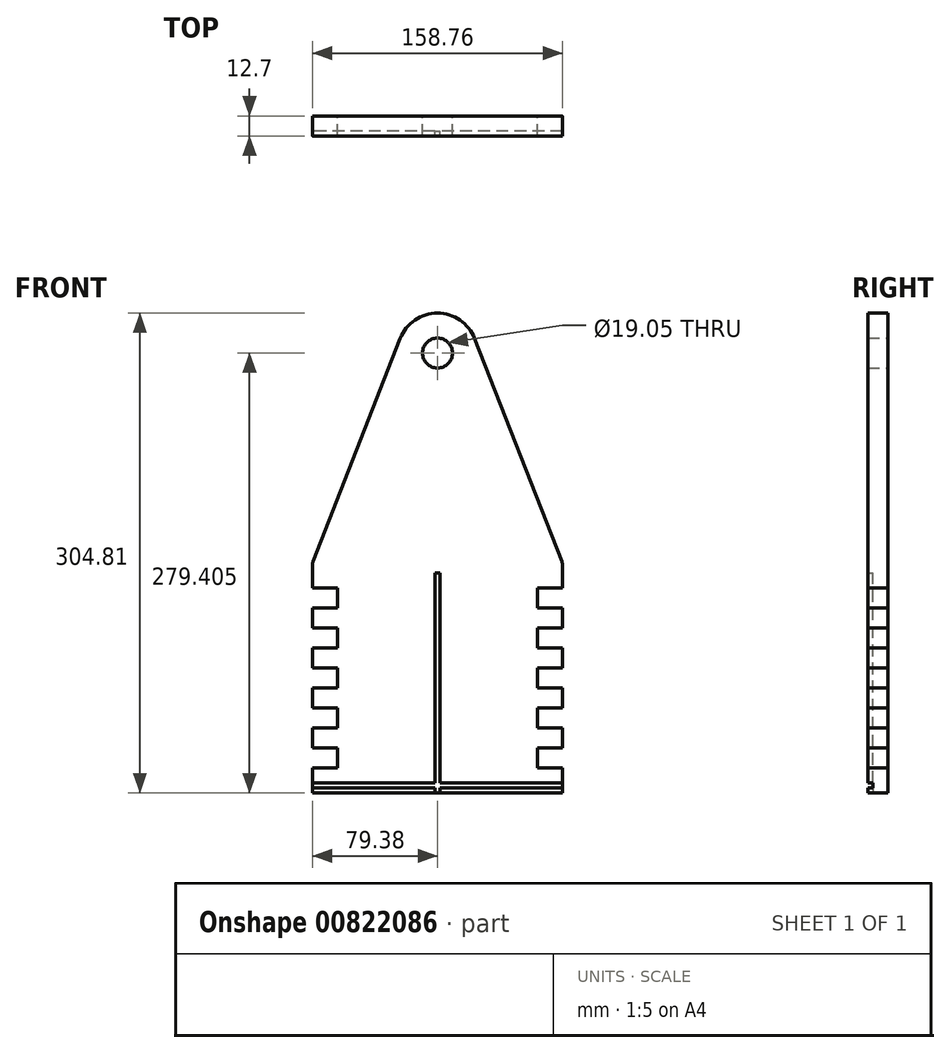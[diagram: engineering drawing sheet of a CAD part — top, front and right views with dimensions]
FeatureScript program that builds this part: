
annotation { "Feature Type Name" : "Feature", "Feature Type Description" : "" }
export const myFeature = defineFeature(function(context is Context, id is Id, definition is map)
    precondition{}
    {
        {
            var Q0;
            Q0=qCreatedBy(makeId("Front.planeOp"),FACE);
            var sketch = newSketch(context, id + "F0", { "sketchPlane" : qUnion([Q0])});
            skLineSegment(sketch, "E0.bottom", {"start": v(-79.38, -73.03) * mm, "end": v(79.38, -73.03) * mm});
            skLineSegment(sketch, "E0.left", {"start": v(-79.37, -73.03) * mm, "end": v(-79.37, -57.15) * mm});
            skLineSegment(sketch, "E0.right", {"start": v(79.38, -73.03) * mm, "end": v(79.38, -57.15) * mm});
            skPoint(sketch, "E0.middle", {"position": v(0, 0) * mm});
            skArc(sketch, "E1", {"start": v(23.66, 215.62) * mm, "mid": v(0, 231.78) * mm, "end": v(-23.66, 215.62) * mm});
            skLineSegment(sketch, "E2.bottom", {"start": v(-79.38, -57.15) * mm, "end": v(-63.5, -57.15) * mm});
            skLineSegment(sketch, "E2.top", {"start": v(-79.38, -44.45) * mm, "end": v(-63.5, -44.45) * mm});
            skLineSegment(sketch, "E2.right", {"start": v(-63.5, -57.15) * mm, "end": v(-63.5, -44.45) * mm});
            skLineSegment(sketch, "E3.0.1.0", {"start": v(-63.5, -31.75) * mm, "end": v(-63.5, -19.05) * mm});
            skLineSegment(sketch, "E3.0.1.2", {"start": v(-79.37, -31.75) * mm, "end": v(-63.5, -31.75) * mm});
            skLineSegment(sketch, "E3.0.1.3", {"start": v(-79.37, -19.05) * mm, "end": v(-63.5, -19.05) * mm});
            skLineSegment(sketch, "E3.0.2.0", {"start": v(-63.5, -6.35) * mm, "end": v(-63.5, 6.35) * mm});
            skLineSegment(sketch, "E3.0.2.2", {"start": v(-79.38, -6.35) * mm, "end": v(-63.5, -6.35) * mm});
            skLineSegment(sketch, "E3.0.2.3", {"start": v(-79.38, 6.35) * mm, "end": v(-63.5, 6.35) * mm});
            skLineSegment(sketch, "E3.0.3.0", {"start": v(-63.5, 19.05) * mm, "end": v(-63.5, 31.75) * mm});
            skLineSegment(sketch, "E3.0.3.2", {"start": v(-79.38, 19.05) * mm, "end": v(-63.5, 19.05) * mm});
            skLineSegment(sketch, "E3.0.3.3", {"start": v(-79.38, 31.75) * mm, "end": v(-63.5, 31.75) * mm});
            skLineSegment(sketch, "E3.0.4.0", {"start": v(-63.5, 44.45) * mm, "end": v(-63.5, 57.15) * mm});
            skLineSegment(sketch, "E3.0.4.2", {"start": v(-79.38, 44.45) * mm, "end": v(-63.5, 44.45) * mm});
            skLineSegment(sketch, "E3.0.4.3", {"start": v(-79.38, 57.15) * mm, "end": v(-63.5, 57.15) * mm});
            skLineSegment(sketch, "E3.direction2", {"start": v(-79.37, -44.45) * mm, "end": v(-79.37, -31.75) * mm, "construction": true});
            skLineSegment(sketch, "E4.MirrorCS", {"start": v(79.38, 44.45) * mm, "end": v(63.5, 44.45) * mm});
            skLineSegment(sketch, "E5.MirrorCS", {"start": v(79.37, -19.05) * mm, "end": v(63.5, -19.05) * mm});
            skLineSegment(sketch, "E6.MirrorCS", {"start": v(79.37, -31.75) * mm, "end": v(63.5, -31.75) * mm});
            skLineSegment(sketch, "E7.MirrorCS", {"start": v(63.5, -31.75) * mm, "end": v(63.5, -19.05) * mm});
            skLineSegment(sketch, "E8.MirrorCS", {"start": v(79.38, 31.75) * mm, "end": v(63.5, 31.75) * mm});
            skLineSegment(sketch, "E9.MirrorCS", {"start": v(79.38, 6.35) * mm, "end": v(63.5, 6.35) * mm});
            skLineSegment(sketch, "E10.MirrorCS", {"start": v(63.5, -57.15) * mm, "end": v(63.5, -44.45) * mm});
            skLineSegment(sketch, "E11.MirrorCS", {"start": v(79.38, -44.45) * mm, "end": v(63.5, -44.45) * mm});
            skLineSegment(sketch, "E12.MirrorCS", {"start": v(79.38, -57.15) * mm, "end": v(63.5, -57.15) * mm});
            skLineSegment(sketch, "E13.MirrorCS", {"start": v(79.38, -6.35) * mm, "end": v(63.5, -6.35) * mm});
            skLineSegment(sketch, "E14.MirrorCS", {"start": v(63.5, 19.05) * mm, "end": v(63.5, 31.75) * mm});
            skLineSegment(sketch, "E15.MirrorCS", {"start": v(63.5, -6.35) * mm, "end": v(63.5, 6.35) * mm});
            skLineSegment(sketch, "E16.MirrorCS", {"start": v(79.38, 19.05) * mm, "end": v(63.5, 19.05) * mm});
            skLineSegment(sketch, "E17.MirrorCS", {"start": v(63.5, 44.45) * mm, "end": v(63.5, 57.15) * mm});
            skLineSegment(sketch, "E18.MirrorCS", {"start": v(79.38, 57.15) * mm, "end": v(63.5, 57.15) * mm});
            skLineSegment(sketch, "E19.MirrorCS", {"start": v(79.37, -44.45) * mm, "end": v(79.37, -31.75) * mm, "construction": true});
            skLineSegment(sketch, "E20.trimOffspring", {"start": v(-79.38, 57.15) * mm, "end": v(-79.38, 71.83) * mm});
            skLineSegment(sketch, "E21.trimOffspring", {"start": v(-79.38, 31.75) * mm, "end": v(-79.38, 44.45) * mm});
            skLineSegment(sketch, "E22.trimOffspring", {"start": v(-79.38, 6.35) * mm, "end": v(-79.38, 19.05) * mm});
            skLineSegment(sketch, "E23.trimOffspring", {"start": v(-79.38, -19.05) * mm, "end": v(-79.38, -6.35) * mm});
            skLineSegment(sketch, "E24.trimOffspring", {"start": v(-79.37, -44.45) * mm, "end": v(-79.37, -31.75) * mm});
            skLineSegment(sketch, "E25.trimOffspring", {"start": v(79.38, -44.45) * mm, "end": v(79.38, -31.75) * mm});
            skLineSegment(sketch, "E26.trimOffspring", {"start": v(79.38, -19.05) * mm, "end": v(79.38, -6.35) * mm});
            skLineSegment(sketch, "E27.trimOffspring", {"start": v(79.38, 6.35) * mm, "end": v(79.38, 19.05) * mm});
            skLineSegment(sketch, "E28.trimOffspring", {"start": v(79.38, 31.75) * mm, "end": v(79.38, 44.45) * mm});
            skLineSegment(sketch, "E29.trimOffspring", {"start": v(79.37, 57.15) * mm, "end": v(79.37, 71.83) * mm});
            skLineSegment(sketch, "E30", {"start": v(-78.94, 74.14) * mm, "end": v(-23.66, 215.62) * mm});
            skLineSegment(sketch, "E31.MirrorCS", {"start": v(78.94, 74.14) * mm, "end": v(23.66, 215.62) * mm});
            skCircle(sketch, "E32", {"center": v(0, 206.38) * mm, "radius": 9.53 * mm});
            skLineSegment(sketch, "E33.bottom", {"start": v(79.38, -69.85) * mm, "end": v(1.55, -69.85) * mm});
            skLineSegment(sketch, "E33.top", {"start": v(79.38, -66.68) * mm, "end": v(1.59, -66.68) * mm});
            skLineSegment(sketch, "E33.left", {"start": v(79.38, -69.85) * mm, "end": v(79.38, -66.68) * mm});
            skLineSegment(sketch, "E33.right", {"start": v(-79.37, -69.85) * mm, "end": v(-79.37, -66.68) * mm});
            skPoint(sketch, "E34.visualSharp", {"position": v(79.38, 73.02) * mm});
            skArc(sketch, "E34.filletArc", {"start": v(79.38, 71.83) * mm, "mid": v(79.27, 73) * mm, "end": v(78.94, 74.14) * mm});
            skPoint(sketch, "E35.visualSharp", {"position": v(-79.38, 73.02) * mm});
            skArc(sketch, "E35.filletArc", {"start": v(-78.94, 74.14) * mm, "mid": v(-79.27, 73) * mm, "end": v(-79.38, 71.83) * mm});
            skLineSegment(sketch, "E36.top", {"start": v(-1.59, 66.68) * mm, "end": v(1.59, 66.68) * mm});
            skLineSegment(sketch, "E36.left", {"start": v(-1.59, -66.68) * mm, "end": v(-1.59, 66.68) * mm});
            skLineSegment(sketch, "E36.right", {"start": v(1.59, -66.68) * mm, "end": v(1.59, 66.68) * mm});
            skLineSegment(sketch, "E37.trimOffspring", {"start": v(-1.59, -66.68) * mm, "end": v(-79.38, -66.68) * mm});
            skLineSegment(sketch, "E38", {"start": v(-1.59, -69.85) * mm, "end": v(-1.59, -73.03) * mm});
            skLineSegment(sketch, "E39", {"start": v(1.55, -69.85) * mm, "end": v(1.55, -73.03) * mm});
            skLineSegment(sketch, "E40.trimOffspring", {"start": v(-1.59, -69.85) * mm, "end": v(-79.38, -69.85) * mm});
            skSolve(sketch);
        }
        {
            var Q0;
            Q0=makeQuery(id+"F0.imprint","IMPRINT",FACE,{"disambiguationData":[TD([[makeQuery(id+"F0.imprint","IMPRINT",EDGE,{"derivedFrom":sQuery(id+"F0.wireOp",EDGE,"E33.bottom")}),-1.0]])]});
            extrude(context, id + "F1", {"entities" : qUnion([Q0]), "depth" : 9.52 * mm, "offsetDistance" : 25.4 * mm});
        }
        {
            var Q0;
            {var subQ0=sQuery(id+"F0.wireOp",EDGE,"E0.bottom");Q0=makeQuery(id+"F0.imprint","IMPRINT",FACE,{"disambiguationData":[TD([[makeQuery(id+"F0.imprint","IMPRINT",EDGE,{"derivedFrom":subQ0}),1.0]])]});}
            var Q1;
            Q1=makeQuery(id+"F0.imprint","IMPRINT",FACE,{"disambiguationData":[TD([[makeQuery(id+"F0.imprint","IMPRINT",EDGE,{"derivedFrom":sQuery(id+"F0.wireOp",EDGE,"E1")}),1.0]])]});
            extrude(context, id + "F2", {"entities" : qUnion([Q0, Q1]), "operationType" : NewBodyOperationType.ADD, "depth" : 12.7 * mm, "offsetDistance" : 25.4 * mm});
        }
    });
